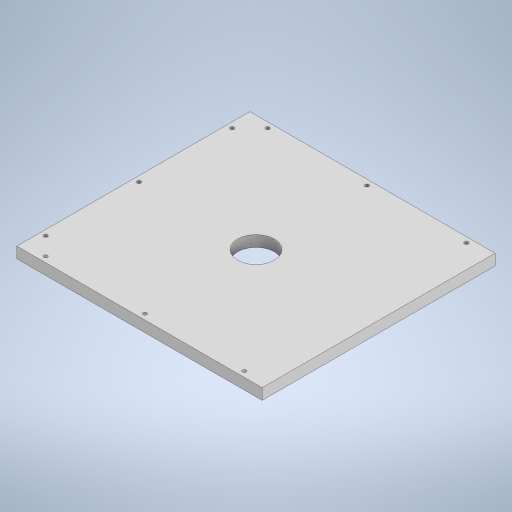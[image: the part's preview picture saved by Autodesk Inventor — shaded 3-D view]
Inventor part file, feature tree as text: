
AUTODESK INVENTOR PART (.ipt)
format: ipt  version: 2023.2 (Build 272271030, 271C)  size: 565,248 bytes
history: native  units: mm
features: extrude x4, sketch x3, projected_geometry x2
ambient origin geometry x8: Origin, YZ Plane, XZ Plane, XY Plane, X Axis, Y Axis, Z Axis, Center Point
bodies: Solid1 (feature_tree)
feature tree (9):
  extrude  "Extrusion1"  Depth=190.0mm
  extrude  "Extrusion10"  Depth=9.0mm
  sketch  "Sketch14"  dims[d28=9.0mm d29=0.0mm d47=9.0mm d48=9.0mm d49=9.0mm d50=3.0mm d51=3.0mm d52=3.0mm d53=10.0mm d54=0.0mm d55=3.0mm d56=3.0mm d57=3.0mm d58=10.0mm d59=0.0mm d60=19.0mm]
  extrude  "Extrusion14"  Depth=9.0mm
  extrude  "Extrusion15"  Depth=9.0mm
  sketch  "Sketch1"  dims[d0=200.0mm d1=190.0mm]
  sketch  "Sketch10"  dims[d2=9.0mm d3=0.0mm d27=30.0mm]
  projected_geometry  "Projected Loop8"
  projected_geometry  "Projected Loop12"
